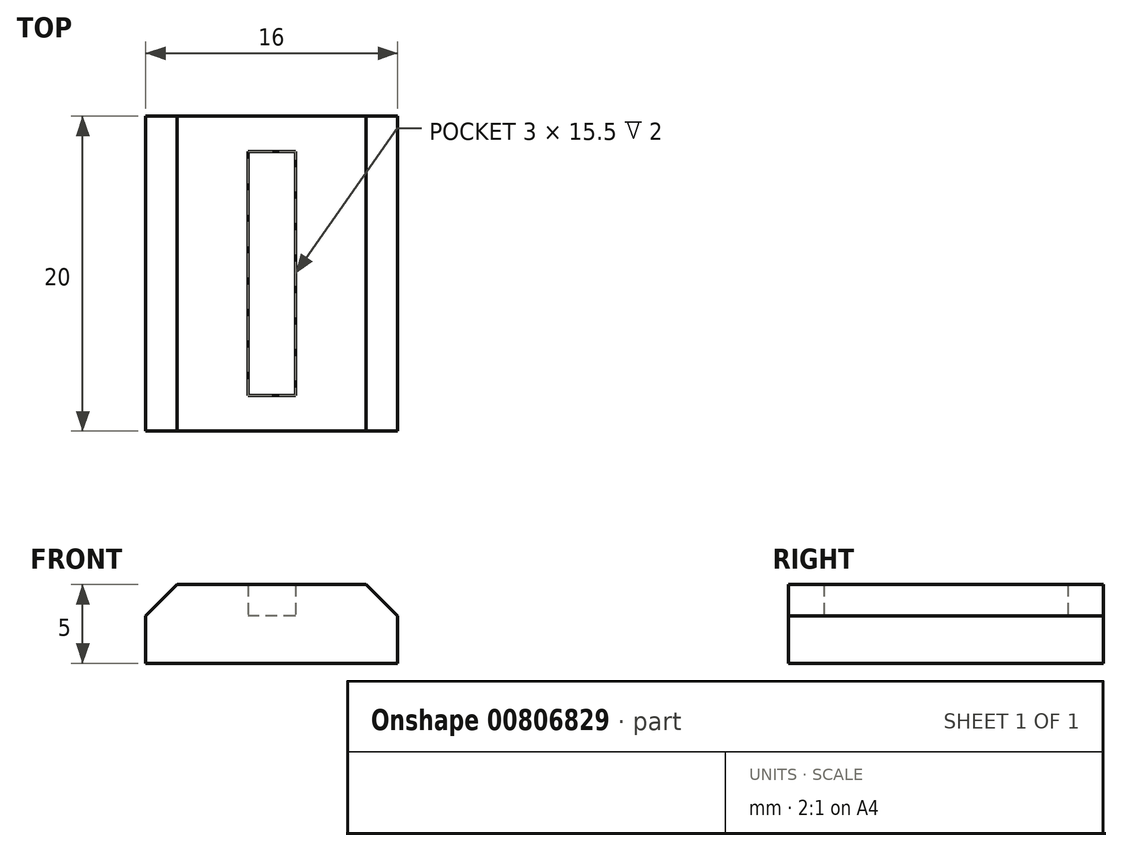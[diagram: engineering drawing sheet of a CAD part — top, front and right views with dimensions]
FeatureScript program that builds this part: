
annotation { "Feature Type Name" : "Feature", "Feature Type Description" : "" }
export const myFeature = defineFeature(function(context is Context, id is Id, definition is map)
    precondition{}
    {
        {
            var Q0;
            Q0=qCreatedBy(makeId("Top.planeOp"),FACE);
            var sketch = newSketch(context, id + "F0", { "sketchPlane" : qUnion([Q0])});
            skLineSegment(sketch, "E0.bottom", {"start": v(8, 10) * mm, "end": v(-8, 10) * mm});
            skLineSegment(sketch, "E0.top", {"start": v(8, -10) * mm, "end": v(-8, -10) * mm});
            skLineSegment(sketch, "E0.left", {"start": v(8, 10) * mm, "end": v(8, -10) * mm});
            skLineSegment(sketch, "E0.right", {"start": v(-8, 10) * mm, "end": v(-8, -10) * mm});
            skPoint(sketch, "E0.middle", {"position": v(0, 0) * mm});
            skLineSegment(sketch, "E1.bottom", {"start": v(1.5, 7.75) * mm, "end": v(-1.5, 7.75) * mm});
            skLineSegment(sketch, "E1.top", {"start": v(1.5, -7.75) * mm, "end": v(-1.5, -7.75) * mm});
            skLineSegment(sketch, "E1.left", {"start": v(1.5, 7.75) * mm, "end": v(1.5, -7.75) * mm});
            skLineSegment(sketch, "E1.right", {"start": v(-1.5, 7.75) * mm, "end": v(-1.5, -7.75) * mm});
            skLineSegment(sketch, "E2", {"start": v(-1.5, 7.75) * mm, "end": v(1.5, -7.75) * mm});
            skSolve(sketch);
        }
        {
            var Q0;
            Q0=makeQuery(id+"F0.imprint","IMPRINT",FACE,{"disambiguationData":[TD([[makeQuery(id+"F0.imprint","IMPRINT",EDGE,{"derivedFrom":sQuery(id+"F0.wireOp",EDGE,"E1.bottom")}),1.0]])]});
            var Q1;
            Q1=makeQuery(id+"F0.imprint","IMPRINT",FACE,{"disambiguationData":[TD([[makeQuery(id+"F0.imprint","IMPRINT",EDGE,{"derivedFrom":sQuery(id+"F0.wireOp",EDGE,"E1.top")}),-1.0]])]});
            extrude(context, id + "F1", {"entities" : qUnion([Q0, Q1]), "depth" : 3 * mm, "offsetDistance" : 25 * mm});
        }
        {
            var Q0;
            Q0=makeQuery(id+"F0.imprint","IMPRINT",FACE,{"disambiguationData":[TD([[makeQuery(id+"F0.imprint","IMPRINT",EDGE,{"derivedFrom":sQuery(id+"F0.wireOp",EDGE,"E0.bottom")}),1.0]])]});
            extrude(context, id + "F2", {"entities" : qUnion([Q0]), "operationType" : NewBodyOperationType.ADD, "depth" : 5 * mm, "offsetDistance" : 25 * mm});
        }
        {
            var Q0;
            Q0=makeQuery(id+"F2.opExtrude","CAP_EDGE",EDGE,{"disambiguationData":[OSD([sQuery(id+"F0.wireOp",EDGE,"E0.left")])],"isStart":false});
            var Q1;
            Q1=makeQuery(id+"F2.opExtrude","CAP_EDGE",EDGE,{"disambiguationData":[OSD([sQuery(id+"F0.wireOp",EDGE,"E0.right")])],"isStart":false});
            chamfer(context, id + "F3", {"entities" : qUnion([Q0, Q1]), "width" : 2 * mm, "tangentPropagation" : true});
        }
    });
